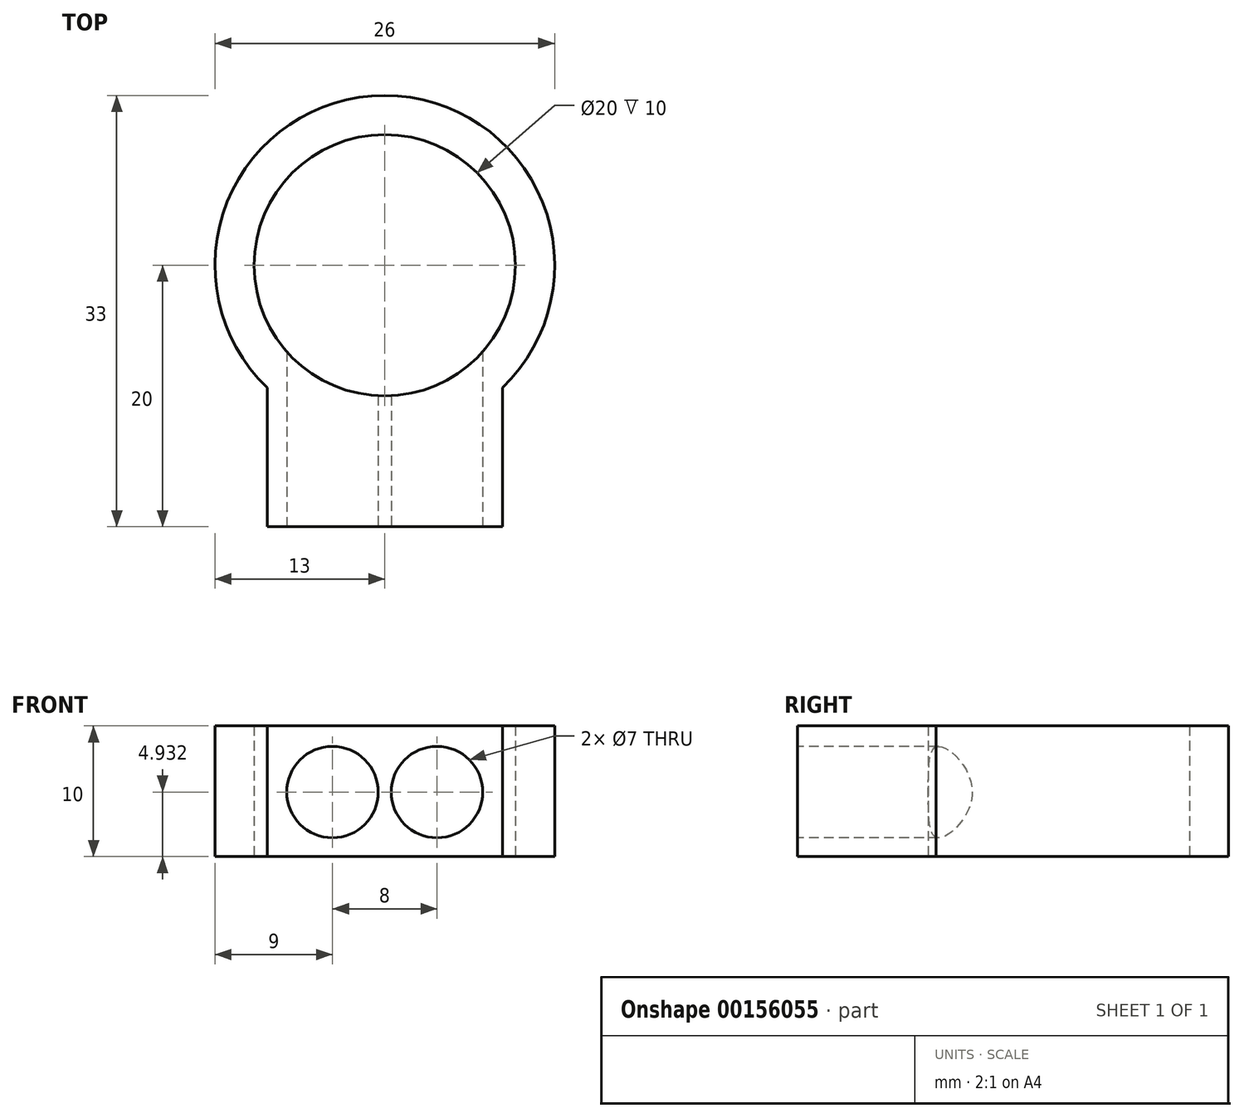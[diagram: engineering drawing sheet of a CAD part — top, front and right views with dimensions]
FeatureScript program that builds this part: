
annotation { "Feature Type Name" : "Feature", "Feature Type Description" : "" }
export const myFeature = defineFeature(function(context is Context, id is Id, definition is map)
    precondition{}
    {
        {
            var Q0;
            Q0=qCreatedBy(makeId("Top.planeOp"),FACE);
            var sketch = newSketch(context, id + "F0", { "sketchPlane" : qUnion([Q0])});
            skCircle(sketch, "E0", {"center": v(0, 0) * mm, "radius": 10 * mm});
            skCircle(sketch, "E1", {"center": v(0, 0) * mm, "radius": 13 * mm});
            skLineSegment(sketch, "E2", {"start": v(-9, -9.38) * mm, "end": v(-9, -20) * mm});
            skLineSegment(sketch, "E3", {"start": v(-9, -20) * mm, "end": v(9, -20) * mm});
            skLineSegment(sketch, "E4", {"start": v(9, -20) * mm, "end": v(9, -9.38) * mm});
            skSolve(sketch);
        }
        {
            var Q0;
            Q0 = qSketchRegion(id + "F0", true);
            extrude(context, id + "F1", {"entities" : qUnion([Q0]), "depth" : 10 * mm});
        }
        {
            var Q0;
            Q0=makeQuery(id+"F1.opExtrude","SWEPT_FACE",FACE,{"disambiguationData":[OSD([sQuery(id+"F0.wireOp",EDGE,"E3")])]});
            var sketch = newSketch(context, id + "F2", { "sketchPlane" : qUnion([Q0])});
            skCircle(sketch, "E5", {"center": v(-4, 4.93) * mm, "radius": 3.5 * mm});
            skCircle(sketch, "E6", {"center": v(4, 4.93) * mm, "radius": 3.5 * mm});
            skLineSegment(sketch, "E7", {"start": v(-4, 4.93) * mm, "end": v(4, 4.93) * mm, "construction": true});
            skSolve(sketch);
        }
        {
            var Q0;
            Q0 = qSketchRegion(id + "F2", true);
            extrude(context, id + "F3", {"entities" : qUnion([Q0]), "operationType" : NewBodyOperationType.REMOVE, "endBound" : BoundingType.UP_TO_NEXT, "oppositeDirection" : true, "depth" : 25 * mm});
        }
    });
